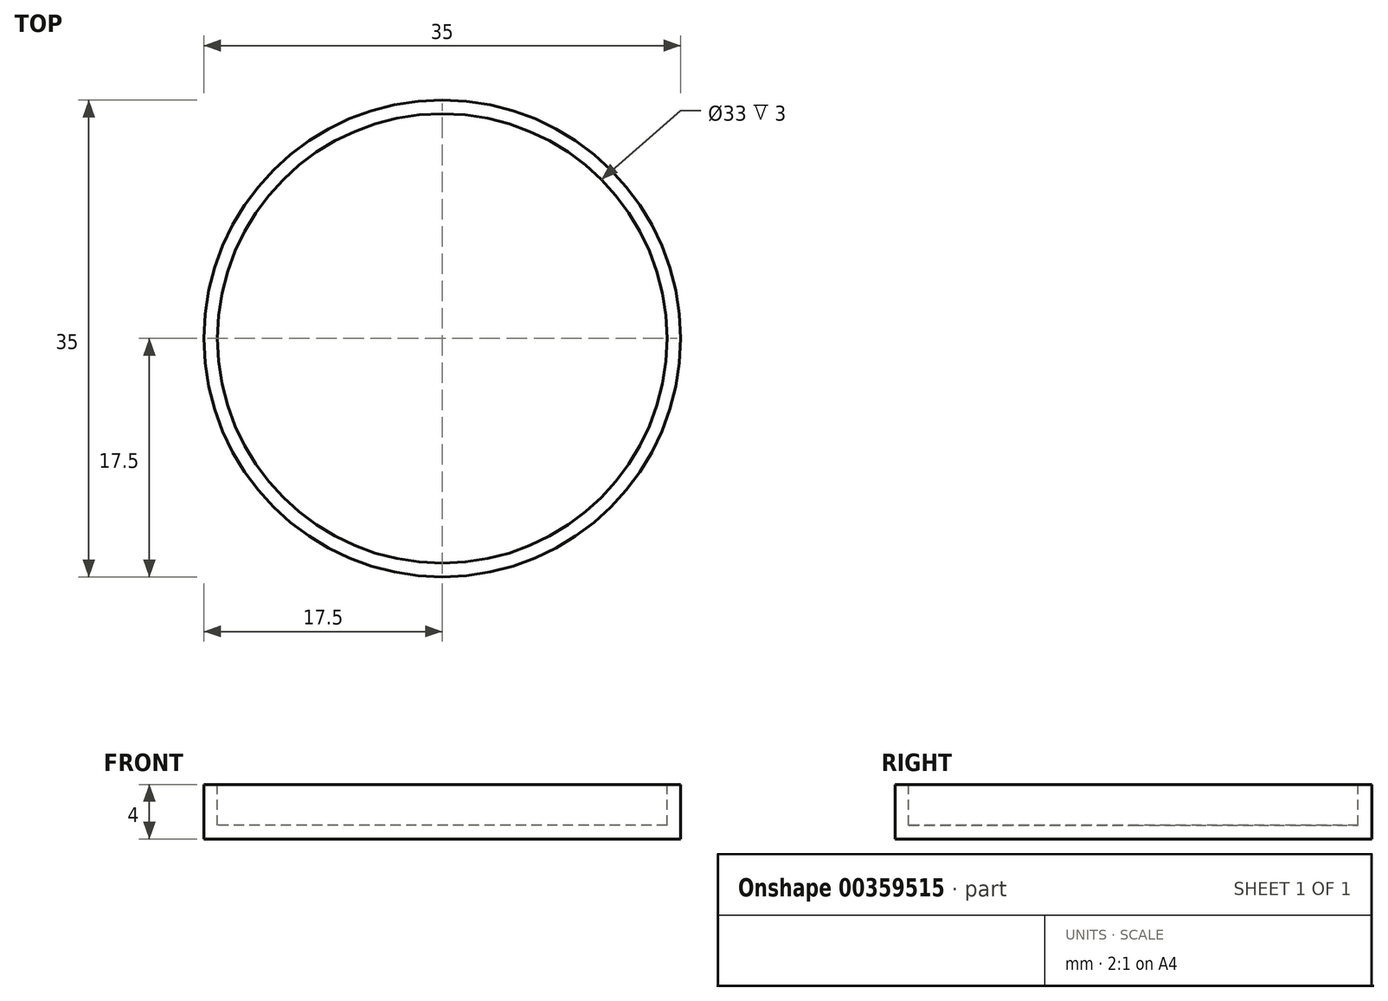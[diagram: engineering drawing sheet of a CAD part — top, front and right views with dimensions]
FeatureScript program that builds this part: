
annotation { "Feature Type Name" : "Feature", "Feature Type Description" : "" }
export const myFeature = defineFeature(function(context is Context, id is Id, definition is map)
    precondition{}
    {
        {
            var Q0;
            Q0=qCreatedBy(makeId("Top.planeOp"),FACE);
            var sketch = newSketch(context, id + "F0", { "sketchPlane" : qUnion([Q0])});
            skCircle(sketch, "E0", {"center": v(0, 0) * mm, "radius": 17.5 * mm});
            skSolve(sketch);
        }
        {
            var Q0;
            Q0=makeQuery(id+"F0.imprint","IMPRINT",FACE,{"disambiguationData":[TD([[makeQuery(id+"F0.imprint","IMPRINT",EDGE,{"derivedFrom":sQuery(id+"F0.wireOp",EDGE,"E0")}),1.0]])]});
            extrude(context, id + "F1", {"entities" : qUnion([Q0]), "depth" : 4 * mm});
        }
        {
            var Q0;
            Q0=makeQuery(id+"F1.opExtrude","CAP_FACE",FACE,{"disambiguationData":[OSD([sQuery(id+"F0.wireOp",EDGE,"E0")])],"isStart":false});
            var sketch = newSketch(context, id + "F2", { "sketchPlane" : qUnion([Q0])});
            skCircle(sketch, "E1", {"center": v(0, 0) * mm, "radius": 16.5 * mm});
            skSolve(sketch);
        }
        {
            var Q0;
            Q0=makeQuery(id+"F2.imprint","IMPRINT",FACE,{"disambiguationData":[TD([[makeQuery(id+"F2.imprint","IMPRINT",EDGE,{"derivedFrom":sQuery(id+"F2.wireOp",EDGE,"E1")}),1.0]])]});
            extrude(context, id + "F3", {"entities" : qUnion([Q0]), "operationType" : NewBodyOperationType.REMOVE, "oppositeDirection" : true, "depth" : 3 * mm});
        }
        {
            var Q0;
            Q0=makeQuery(id+"F3.boolean.opBoolean","COPY",FACE,{"derivedFrom":makeQuery(id+"F3.opExtrude","CAP_FACE",FACE,{"disambiguationData":[OSD([sQuery(id+"F2.wireOp",EDGE,"E1")])],"isStart":false})});
            var sketch = newSketch(context, id + "F4", { "sketchPlane" : qUnion([Q0])});
            skCircle(sketch, "E2", {"center": v(0, 0) * mm, "radius": 3.5 * mm});
            skCircle(sketch, "E3", {"center": v(0, 0) * mm, "radius": 1.5 * mm});
            skSolve(sketch);
        }
        {
            var Q0;
            Q0=sQuery(id+"F4.wireOp",EDGE,"E2");
            extrude(context, id + "F5", {"bodyType" : ToolBodyType.SURFACE, "surfaceEntities" : qUnion([Q0]), "depth" : 25 * mm});
        }
    });
